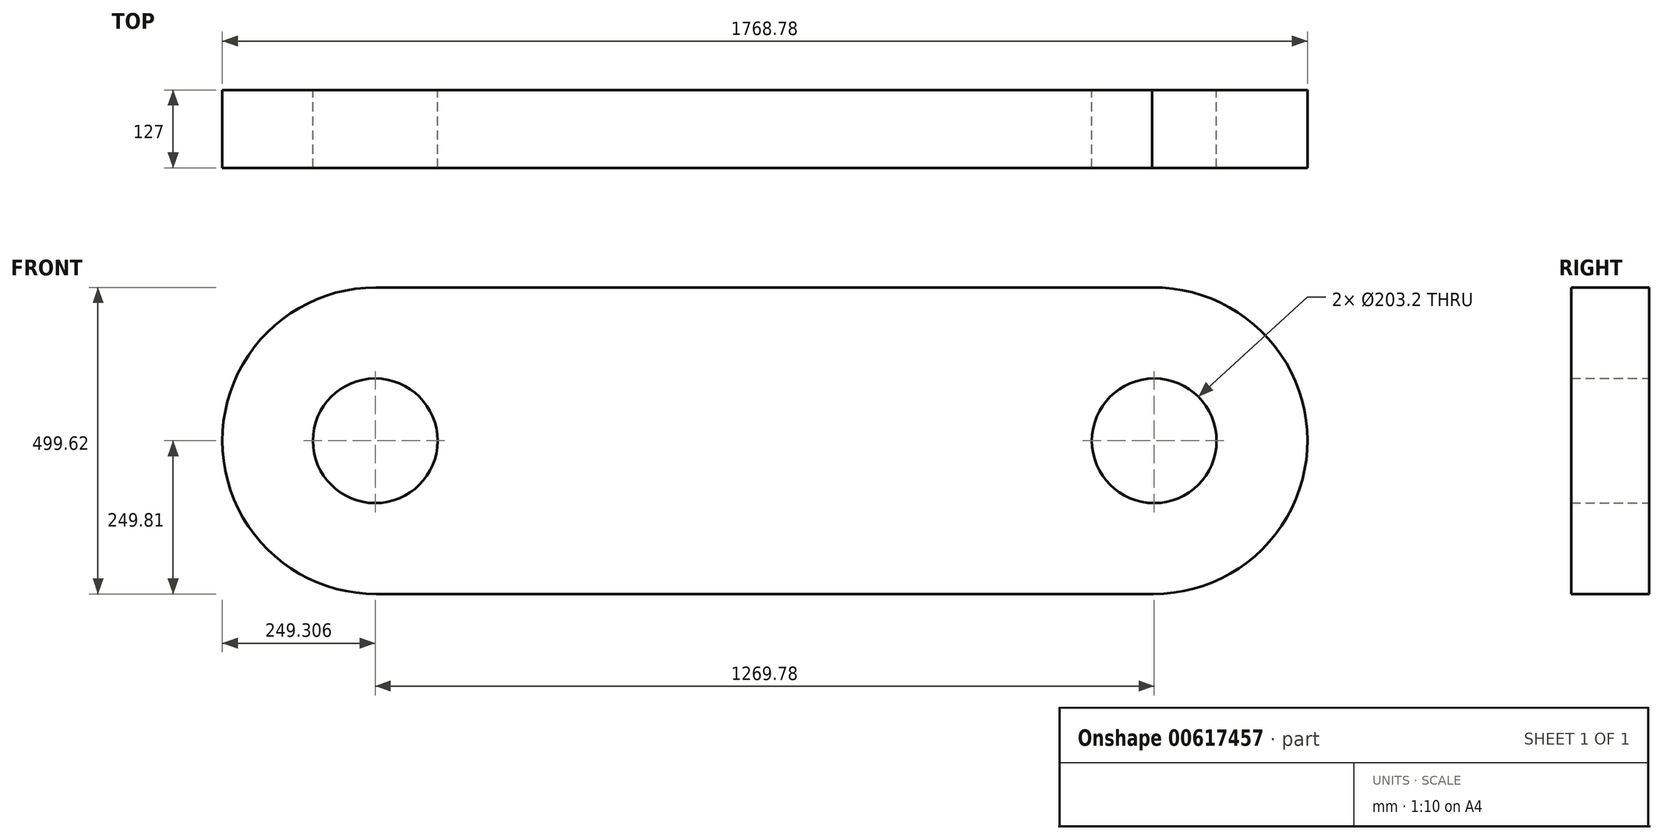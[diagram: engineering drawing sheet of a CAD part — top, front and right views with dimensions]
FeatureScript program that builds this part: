
annotation { "Feature Type Name" : "Feature", "Feature Type Description" : "" }
export const myFeature = defineFeature(function(context is Context, id is Id, definition is map)
    precondition{}
    {
        {
            var Q0;
            Q0=qCreatedBy(makeId("Front.planeOp"),FACE);
            var sketch = newSketch(context, id + "F0", { "sketchPlane" : qUnion([Q0])});
            skLineSegment(sketch, "E0", {"start": v(-595.23, 0) * mm, "end": v(674.77, 0) * mm});
            skCircle(sketch, "E1", {"center": v(-595.23, 0) * mm, "radius": 249.8 * mm});
            skCircle(sketch, "E2", {"center": v(673.93, 0) * mm, "radius": 249.8 * mm});
            skCircle(sketch, "E3", {"center": v(-595.73, 0) * mm, "radius": 101.6 * mm});
            skCircle(sketch, "E4", {"center": v(674.04, 0) * mm, "radius": 101.6 * mm});
            skLineSegment(sketch, "E5", {"start": v(677.26, 249.79) * mm, "end": v(-594.84, 249.8) * mm});
            skLineSegment(sketch, "E6", {"start": v(675.22, -249.8) * mm, "end": v(-594.02, -249.8) * mm});
            skSolve(sketch);
        }
        {
            var Q0;
            Q0 = qSketchRegion(id + "F0", true);
            extrude(context, id + "F1", {"entities" : qUnion([Q0]), "depth" : 127 * mm, "offsetDistance" : 25.4 * mm});
        }
    });
